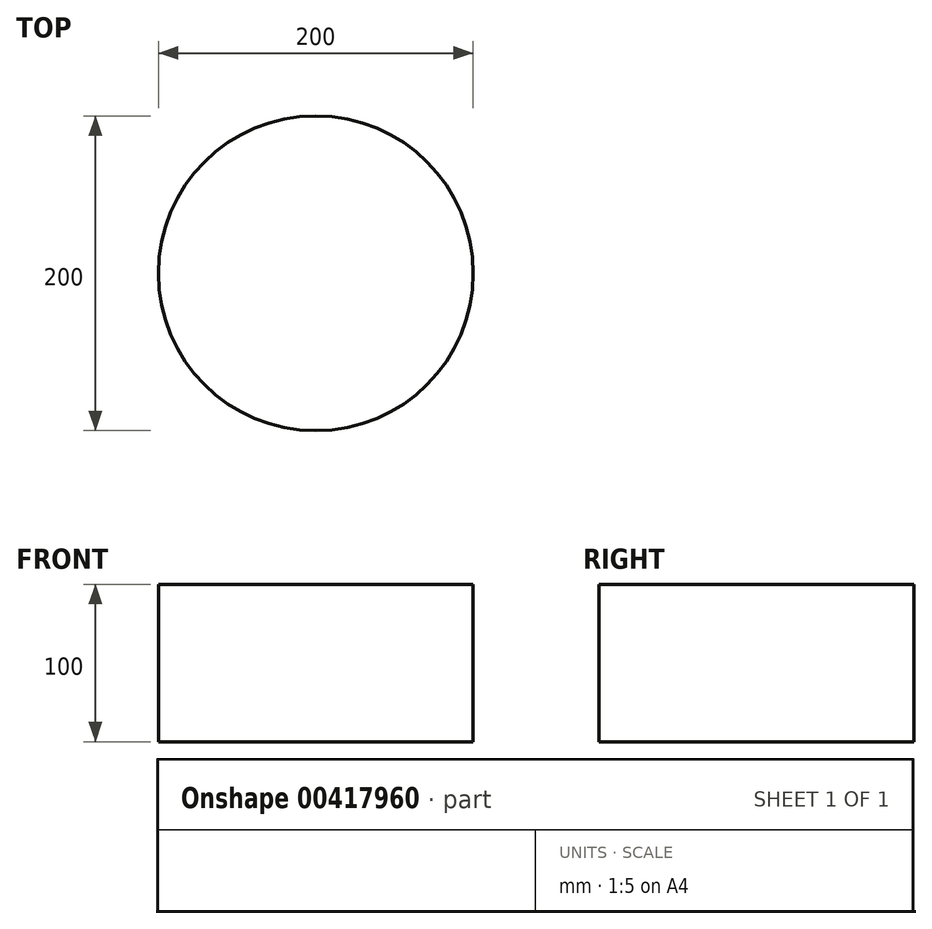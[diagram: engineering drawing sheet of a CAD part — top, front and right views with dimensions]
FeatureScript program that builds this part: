
annotation { "Feature Type Name" : "Feature", "Feature Type Description" : "" }
export const myFeature = defineFeature(function(context is Context, id is Id, definition is map)
    precondition{}
    {
        {
            var Q0;
            Q0=qCreatedBy(makeId("Top.planeOp"),FACE);
            var sketch = newSketch(context, id + "F0", { "sketchPlane" : qUnion([Q0])});
            skCircle(sketch, "E0", {"center": v(0, 0) * mm, "radius": 100 * mm});
            skSolve(sketch);
        }
        {
            var Q0;
            Q0=makeQuery(id+"F0.imprint","IMPRINT",FACE,{"disambiguationData":[TD([[makeQuery(id+"F0.imprint","IMPRINT",EDGE,{"derivedFrom":sQuery(id+"F0.wireOp",EDGE,"E0")}),1.0]])]});
            extrude(context, id + "F1", {"entities" : qUnion([Q0]), "depth" : 100 * mm});
        }
    });
